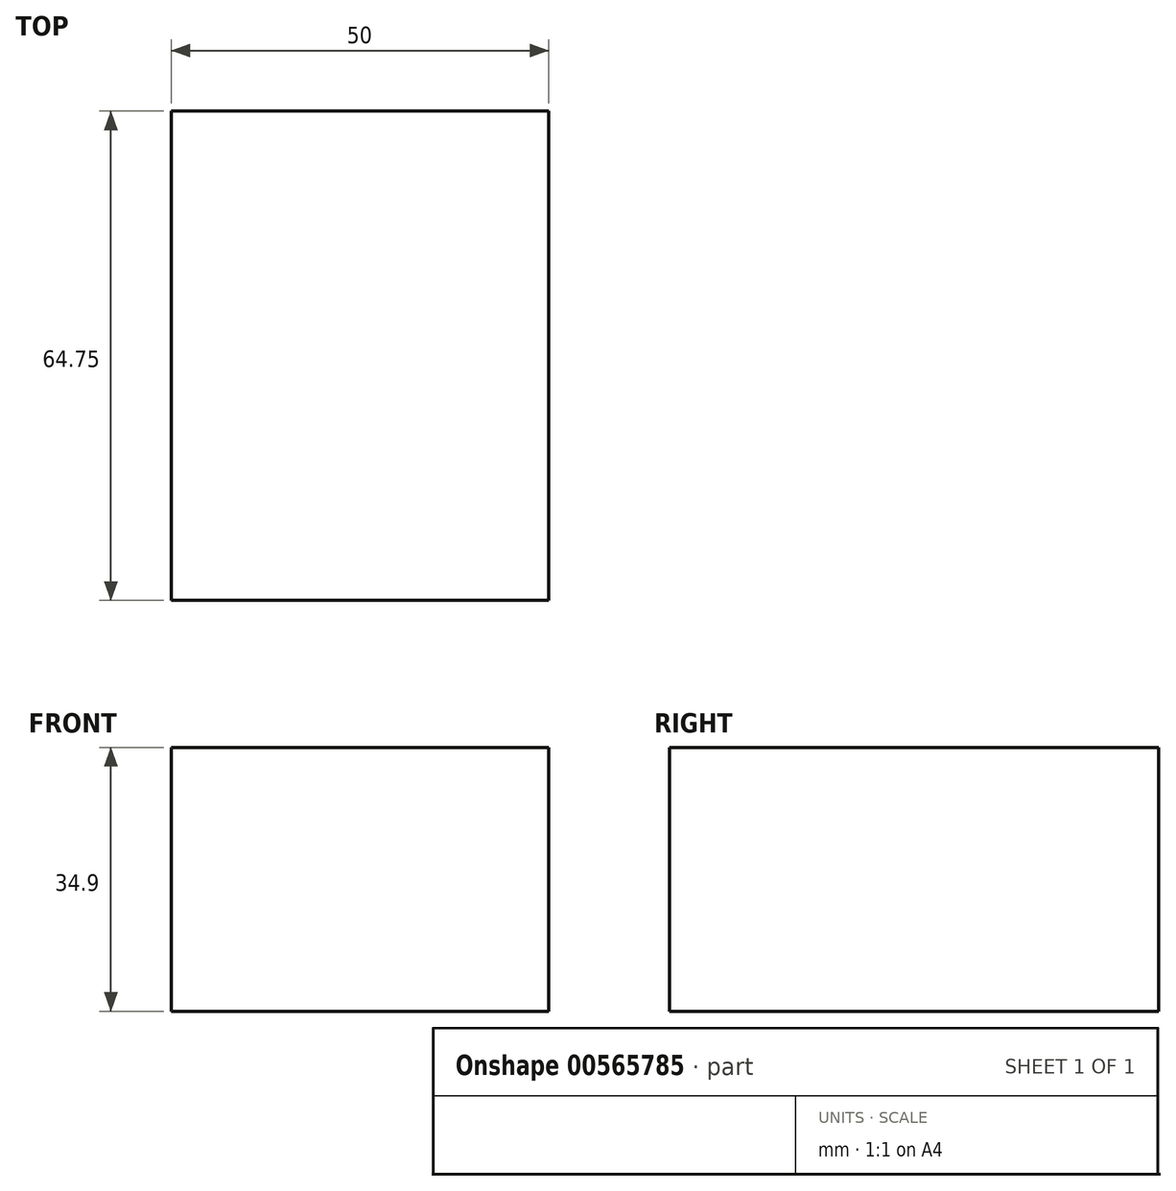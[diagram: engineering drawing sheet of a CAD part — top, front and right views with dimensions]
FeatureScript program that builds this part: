
annotation { "Feature Type Name" : "Feature", "Feature Type Description" : "" }
export const myFeature = defineFeature(function(context is Context, id is Id, definition is map)
    precondition{}
    {
        {
            var Q0;
            Q0=qCreatedBy(makeId("Right.planeOp"),FACE);
            var sketch = newSketch(context, id + "F0", { "sketchPlane" : qUnion([Q0])});
            skLineSegment(sketch, "E0.bottom", {"start": v(0, 0) * mm, "end": v(64.75, 0) * mm});
            skLineSegment(sketch, "E0.top", {"start": v(0, 34.9) * mm, "end": v(64.75, 34.9) * mm});
            skLineSegment(sketch, "E0.left", {"start": v(0, 0) * mm, "end": v(0, 34.9) * mm});
            skLineSegment(sketch, "E0.right", {"start": v(64.75, 0) * mm, "end": v(64.75, 34.9) * mm});
            skSolve(sketch);
        }
        {
            var Q0;
            Q0 = qSketchRegion(id + "F0", true);
            extrude(context, id + "F1", {"entities" : qUnion([Q0]), "depth" : 25 * mm, "offsetDistance" : 25 * mm, "hasSecondDirection" : true, "secondDirectionOppositeDirection" : true, "secondDirectionDepth" : 25 * mm});
        }
    });
